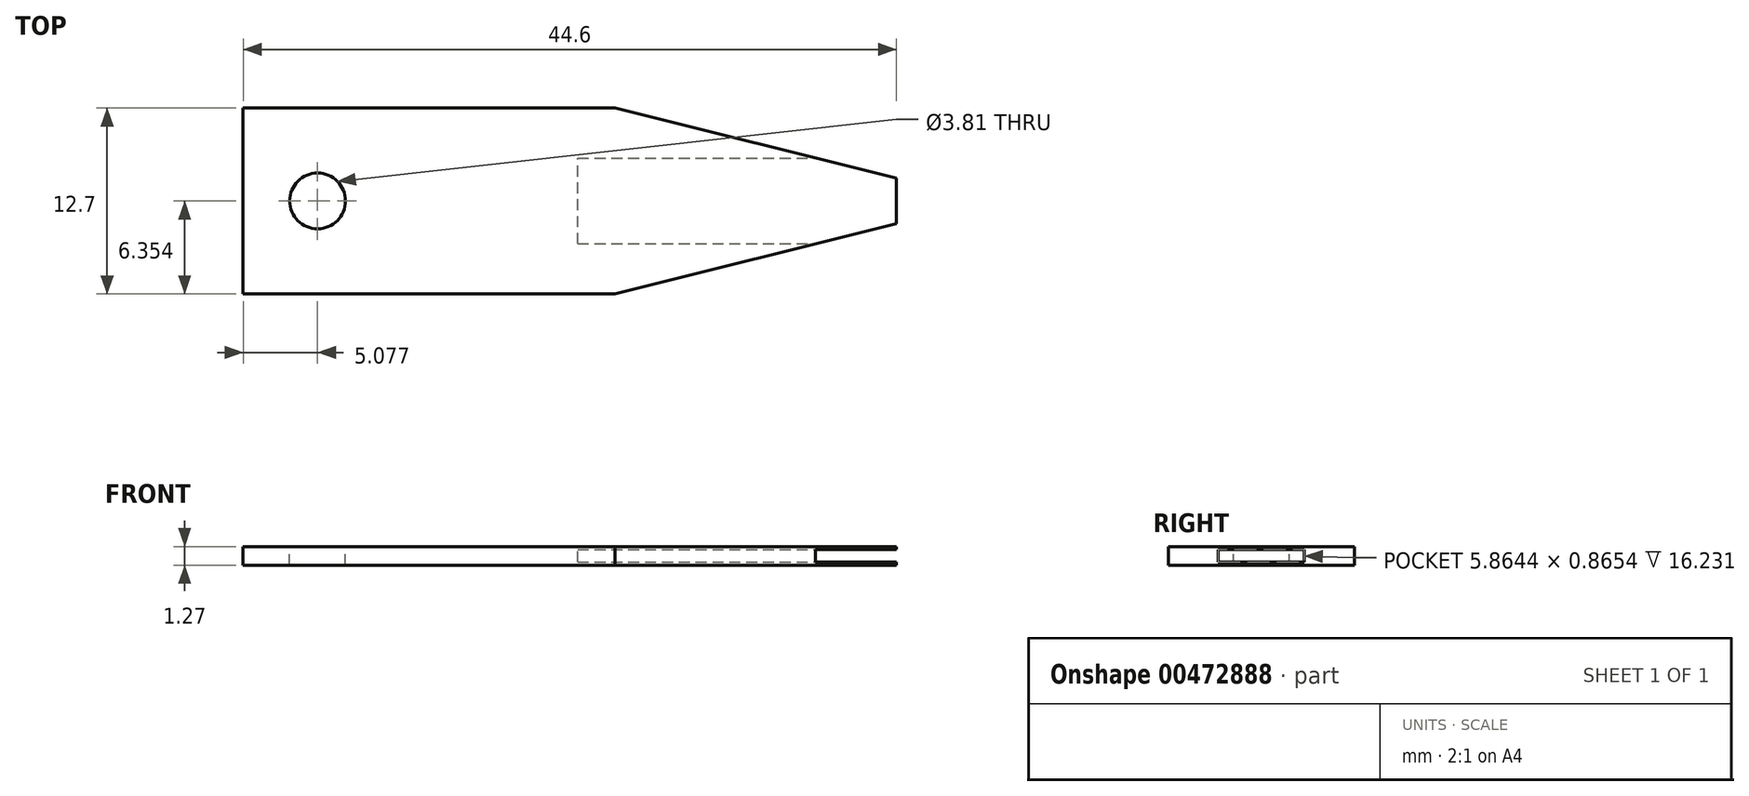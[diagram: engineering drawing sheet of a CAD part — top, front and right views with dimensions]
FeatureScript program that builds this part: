
annotation { "Feature Type Name" : "Feature", "Feature Type Description" : "" }
export const myFeature = defineFeature(function(context is Context, id is Id, definition is map)
    precondition{}
    {
        {
            var Q0;
            Q0=qCreatedBy(makeId("Top.planeOp"),FACE);
            var sketch = newSketch(context, id + "F0", { "sketchPlane" : qUnion([Q0])});
            skLineSegment(sketch, "E0.bottom", {"start": v(18.06, -27.4) * mm, "end": v(68.86, -27.4) * mm});
            skLineSegment(sketch, "E0.top", {"start": v(18.06, -14.7) * mm, "end": v(68.86, -14.7) * mm});
            skLineSegment(sketch, "E0.left", {"start": v(18.06, -27.4) * mm, "end": v(18.06, -14.7) * mm});
            skLineSegment(sketch, "E0.right", {"start": v(68.86, -27.4) * mm, "end": v(68.86, -14.7) * mm});
            skSolve(sketch);
        }
        {
            var Q0;
            Q0=makeQuery(id+"F0.imprint","IMPRINT",FACE,{"disambiguationData":[TD([[makeQuery(id+"F0.imprint","IMPRINT",EDGE,{"derivedFrom":sQuery(id+"F0.wireOp",EDGE,"E0.bottom")}),1.0]])]});
            extrude(context, id + "F1", {"entities" : qUnion([Q0]), "depth" : 1.27 * mm});
        }
        {
            var Q0;
            Q0=makeQuery(id+"F1.opExtrude","CAP_FACE",FACE,{"disambiguationData":[OSD([sQuery(id+"F0.wireOp",EDGE,"E0.bottom"),sQuery(id+"F0.wireOp",EDGE,"E0.top"),sQuery(id+"F0.wireOp",EDGE,"E0.left"),sQuery(id+"F0.wireOp",EDGE,"E0.right")])],"isStart":false});
            var sketch = newSketch(context, id + "F2", { "sketchPlane" : qUnion([Q0])});
            skCircle(sketch, "E1", {"center": v(23.14, -21.06) * mm, "radius": 1.9 * mm});
            skSolve(sketch);
        }
        {
            var Q0;
            Q0=makeQuery(id+"F2.imprint","IMPRINT",FACE,{"disambiguationData":[TD([[makeQuery(id+"F2.imprint","IMPRINT",EDGE,{"derivedFrom":sQuery(id+"F2.wireOp",EDGE,"E1")}),1.0]])]});
            extrude(context, id + "F3", {"entities" : qUnion([Q0]), "operationType" : NewBodyOperationType.REMOVE, "oppositeDirection" : true, "depth" : 25.4 * mm});
        }
        {
            var Q0;
            Q0=makeQuery(id+"F1.opExtrude","CAP_FACE",FACE,{"disambiguationData":[OSD([sQuery(id+"F0.wireOp",EDGE,"E0.bottom"),sQuery(id+"F0.wireOp",EDGE,"E0.top"),sQuery(id+"F0.wireOp",EDGE,"E0.left"),sQuery(id+"F0.wireOp",EDGE,"E0.right")])],"isStart":false});
            var sketch = newSketch(context, id + "F4", { "sketchPlane" : qUnion([Q0])});
            skLineSegment(sketch, "E2", {"start": v(43.46, -27.4) * mm, "end": v(68.86, -21.06) * mm});
            skLineSegment(sketch, "E3", {"start": v(68.86, -21.06) * mm, "end": v(43.46, -14.7) * mm});
            skSolve(sketch);
        }
        {
            var Q0;
            {var subQ0=sQuery(id+"F4.wireOp",EDGE,"E3");Q0=makeQuery(id+"F4.imprint","IMPRINT",FACE,{"disambiguationData":[TD([[makeQuery(id+"F4.imprint","IMPRINT",EDGE,{"derivedFrom":subQ0}),-1.0]])]});}
            var Q1;
            {var subQ0=sQuery(id+"F4.wireOp",EDGE,"E2");Q1=makeQuery(id+"F4.imprint","IMPRINT",FACE,{"disambiguationData":[TD([[makeQuery(id+"F4.imprint","IMPRINT",EDGE,{"derivedFrom":subQ0}),-1.0]])]});}
            extrude(context, id + "F5", {"entities" : qUnion([Q0, Q1]), "operationType" : NewBodyOperationType.REMOVE, "oppositeDirection" : true, "depth" : 25.4 * mm});
        }
        {
            var Q0;
            Q0=makeQuery(id+"F1.opExtrude","CAP_FACE",FACE,{"disambiguationData":[OSD([sQuery(id+"F0.wireOp",EDGE,"E0.bottom"),sQuery(id+"F0.wireOp",EDGE,"E0.top"),sQuery(id+"F0.wireOp",EDGE,"E0.left"),sQuery(id+"F0.wireOp",EDGE,"E0.right")])],"isStart":false});
            var sketch = newSketch(context, id + "F6", { "sketchPlane" : qUnion([Q0])});
            skLineSegment(sketch, "E4.bottom", {"start": v(68.86, -34.9) * mm, "end": v(66.3, -34.9) * mm});
            skLineSegment(sketch, "E4.top", {"start": v(68.86, -6.83) * mm, "end": v(66.3, -6.83) * mm});
            skLineSegment(sketch, "E4.left", {"start": v(68.86, -34.9) * mm, "end": v(68.86, -6.83) * mm});
            skLineSegment(sketch, "E4.right", {"start": v(66.3, -34.9) * mm, "end": v(66.3, -6.83) * mm});
            skSolve(sketch);
        }
        {
            var Q0;
            {var subQ0=sQuery(id+"F6.wireOp",EDGE,"E4.bottom");Q0=makeQuery(id+"F6.imprint","IMPRINT",FACE,{"disambiguationData":[TD([[makeQuery(id+"F6.imprint","IMPRINT",EDGE,{"derivedFrom":subQ0}),-1.0]])]});}
            var Q1;
            {var subQ0=sQuery(id+"F6.wireOp",EDGE,"E4.right");var subQ1=makeQuery(id+"F5.boolean.opBoolean","COPY",EDGE,{"derivedFrom":makeQuery(id+"F5.opExtrude","CAP_EDGE",EDGE,{"disambiguationData":[OSD([sQuery(id+"F4.wireOp",EDGE,"E2")])],"isStart":true})});var subQ2=makeQuery(id+"F6.imprint","INTERSECT",VERTEX,{"derivedFrom":[subQ1,subQ0]});Q1=makeQuery(id+"F6.imprint","IMPRINT",FACE,{"disambiguationData":[TD([[makeQuery(id+"F6.imprint","IMPRINT",EDGE,{"disambiguationData":[TD([[subQ2,-1.0]])],"derivedFrom":subQ0}),-1.0]])]});}
            var Q2;
            {var subQ0=sQuery(id+"F6.wireOp",EDGE,"E4.top");Q2=makeQuery(id+"F6.imprint","IMPRINT",FACE,{"disambiguationData":[TD([[makeQuery(id+"F6.imprint","IMPRINT",EDGE,{"derivedFrom":subQ0}),1.0]])]});}
            extrude(context, id + "F7", {"entities" : qUnion([Q0, Q1, Q2]), "operationType" : NewBodyOperationType.REMOVE, "oppositeDirection" : true, "depth" : 25.4 * mm});
        }
        {
            var Q0;
            Q0=makeQuery(id+"F7.boolean.opBoolean","COPY",FACE,{"derivedFrom":makeQuery(id+"F7.opExtrude","SWEPT_FACE",FACE,{"disambiguationData":[OSD([sQuery(id+"F6.wireOp",EDGE,"E4.right")])]})});
            var sketch = newSketch(context, id + "F8", { "sketchPlane" : qUnion([Q0])});
            skLineSegment(sketch, "E5.bottom", {"start": v(-21.45, 0.2) * mm, "end": v(-20.66, 0.2) * mm});
            skLineSegment(sketch, "E5.top", {"start": v(-21.45, 1.07) * mm, "end": v(-20.66, 1.07) * mm});
            skLineSegment(sketch, "E5.left", {"start": v(-21.45, 0.2) * mm, "end": v(-21.45, 1.07) * mm});
            skLineSegment(sketch, "E5.right", {"start": v(-20.66, 0.2) * mm, "end": v(-20.66, 1.07) * mm});
            skPoint(sketch, "E5.middle", {"position": v(-21.06, 0.64) * mm});
            skPoint(sketch, "E5.middle.positionSnap0", {"position": v(-21.06, 0) * mm});
            skPoint(sketch, "E5.middle.positionSnap1", {"position": v(-21.7, 0.64) * mm});
            skPoint(sketch, "E5.centerSnap0", {"position": v(-21.06, 0) * mm});
            skPoint(sketch, "E5.centerSnap1", {"position": v(-21.7, 0.64) * mm});
            skSolve(sketch);
        }
        {
            var Q0;
            Q0=makeQuery(id+"F8.imprint","IMPRINT",FACE,{"disambiguationData":[TD([[makeQuery(id+"F8.imprint","IMPRINT",EDGE,{"derivedFrom":sQuery(id+"F8.wireOp",EDGE,"E5.bottom")}),1.0]])]});
            extrude(context, id + "F9", {"entities" : qUnion([Q0]), "operationType" : NewBodyOperationType.REMOVE, "oppositeDirection" : true, "depth" : 25.4 * mm});
        }
        {
            var Q0;
            Q0=makeQuery(id+"F1.opExtrude","CAP_FACE",FACE,{"disambiguationData":[OSD([sQuery(id+"F0.wireOp",EDGE,"E0.bottom"),sQuery(id+"F0.wireOp",EDGE,"E0.top"),sQuery(id+"F0.wireOp",EDGE,"E0.left"),sQuery(id+"F0.wireOp",EDGE,"E0.right")])],"isStart":false});
            var sketch = newSketch(context, id + "F10", { "sketchPlane" : qUnion([Q0])});
            skLineSegment(sketch, "E6.bottom", {"start": v(62.66, -16.83) * mm, "end": v(66.3, -16.83) * mm});
            skLineSegment(sketch, "E6.top", {"start": v(62.66, -26.58) * mm, "end": v(66.3, -26.58) * mm});
            skLineSegment(sketch, "E6.left", {"start": v(62.66, -16.83) * mm, "end": v(62.66, -26.58) * mm});
            skLineSegment(sketch, "E6.right", {"start": v(66.3, -16.83) * mm, "end": v(66.3, -26.58) * mm});
            skSolve(sketch);
        }
        {
            var Q0;
            {var subQ0=sQuery(id+"F10.wireOp",EDGE,"E6.left");var subQ1=makeQuery(id+"F5.boolean.opBoolean","COPY",EDGE,{"derivedFrom":makeQuery(id+"F5.opExtrude","CAP_EDGE",EDGE,{"disambiguationData":[OSD([sQuery(id+"F4.wireOp",EDGE,"E3")])],"isStart":true})});var subQ2=makeQuery(id+"F10.imprint","INTERSECT",VERTEX,{"derivedFrom":[subQ1,subQ0]});Q0=makeQuery(id+"F10.imprint","IMPRINT",FACE,{"disambiguationData":[TD([[makeQuery(id+"F10.imprint","IMPRINT",EDGE,{"disambiguationData":[TD([[subQ2,-1.0]])],"derivedFrom":subQ0}),1.0]])]});}
            extrude(context, id + "F11", {"entities" : qUnion([Q0]), "operationType" : NewBodyOperationType.REMOVE, "oppositeDirection" : true, "depth" : 25.4 * mm});
        }
        {
            var Q0;
            Q0=makeQuery(id+"F9.boolean.opBoolean","COPY",FACE,{"derivedFrom":makeQuery(id+"F9.opExtrude","SWEPT_FACE",FACE,{"disambiguationData":[OSD([sQuery(id+"F8.wireOp",EDGE,"E5.right")])]})});
            extrude(context, id + "F12", {"entities" : qUnion([Q0]), "operationType" : NewBodyOperationType.REMOVE, "oppositeDirection" : true, "depth" : 2.54 * mm});
        }
        {
            var Q0;
            Q0=makeQuery(id+"F9.boolean.opBoolean","COPY",FACE,{"derivedFrom":makeQuery(id+"F9.opExtrude","SWEPT_FACE",FACE,{"disambiguationData":[OSD([sQuery(id+"F8.wireOp",EDGE,"E5.left")])]})});
            extrude(context, id + "F13", {"entities" : qUnion([Q0]), "operationType" : NewBodyOperationType.REMOVE, "oppositeDirection" : true, "depth" : 2.54 * mm});
        }
    });
